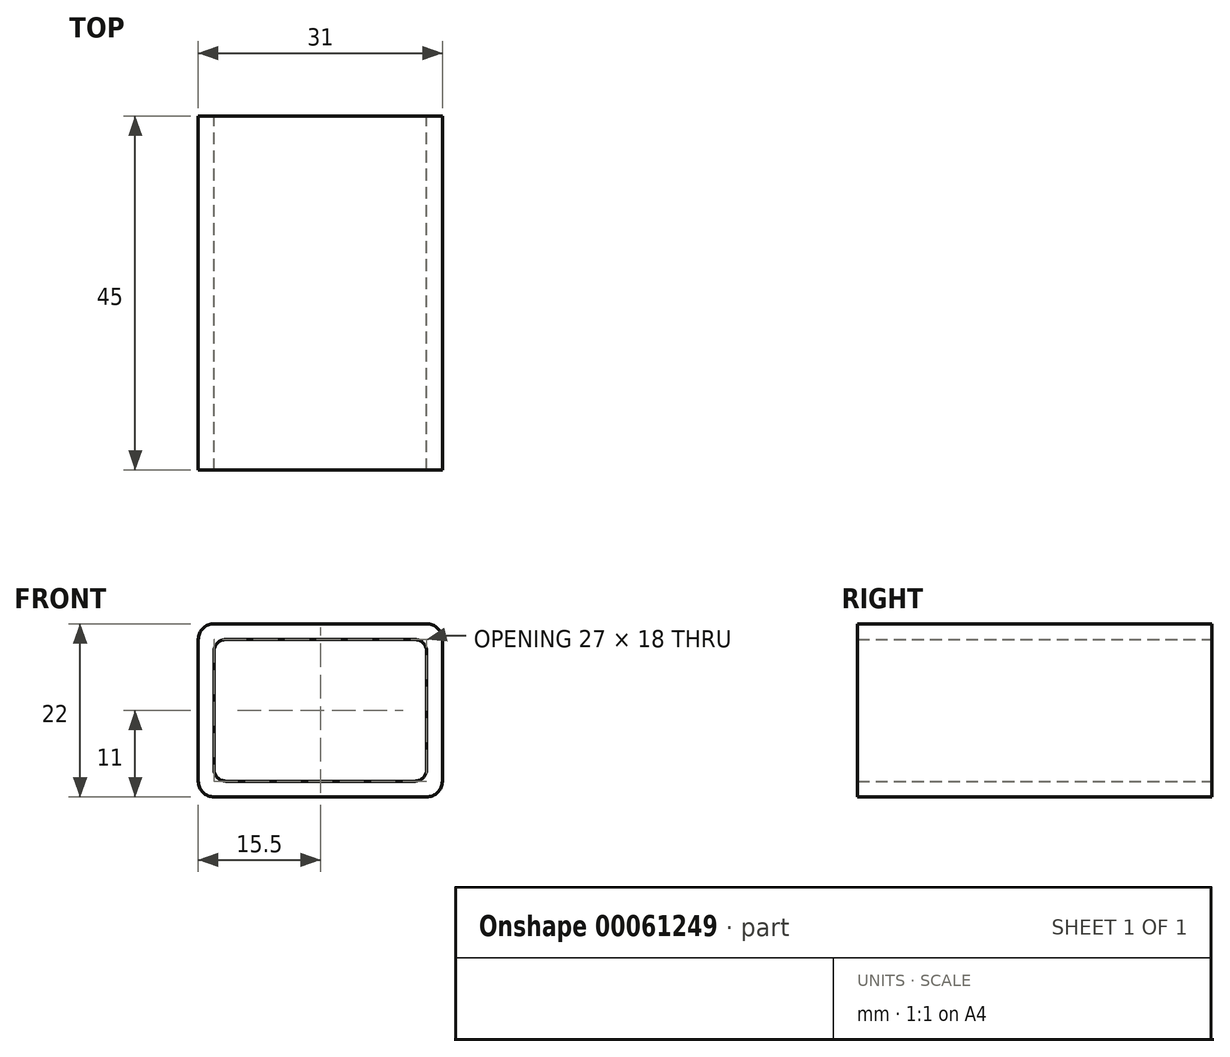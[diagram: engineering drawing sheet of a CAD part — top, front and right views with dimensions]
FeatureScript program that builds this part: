
annotation { "Feature Type Name" : "Feature", "Feature Type Description" : "" }
export const myFeature = defineFeature(function(context is Context, id is Id, definition is map)
    precondition{}
    {
        {
            var Q0;
            Q0=qCreatedBy(makeId("Front.planeOp"),FACE);
            var sketch = newSketch(context, id + "F0", { "sketchPlane" : qUnion([Q0])});
            skLineSegment(sketch, "E0.bottom", {"start": v(0, 0) * mm, "end": v(27, 0) * mm});
            skLineSegment(sketch, "E0.top", {"start": v(0, 18) * mm, "end": v(27, 18) * mm});
            skLineSegment(sketch, "E0.left", {"start": v(0, 0) * mm, "end": v(0, 18) * mm});
            skLineSegment(sketch, "E0.right", {"start": v(27, 0) * mm, "end": v(27, 18) * mm});
            skLineSegment(sketch, "E1.0", {"start": v(-2, 20) * mm, "end": v(29, 20) * mm});
            skLineSegment(sketch, "E1.1", {"start": v(-2, -2) * mm, "end": v(-2, 20) * mm});
            skLineSegment(sketch, "E1.2", {"start": v(-2, -2) * mm, "end": v(29, -2) * mm});
            skLineSegment(sketch, "E1.3", {"start": v(29, -2) * mm, "end": v(29, 20) * mm});
            skSolve(sketch);
        }
        {
            var Q0;
            Q0 = qSketchRegion(id + "F0", true);
            extrude(context, id + "F1", {"entities" : qUnion([Q0]), "depth" : 45 * mm});
        }
        {
            var Q0;
            Q0=makeQuery(id+"F1.opExtrude","SWEPT_EDGE",EDGE,{"disambiguationData":[OSD([sQuery(id+"F0.wireOp",EDGE,"E1.0"),sQuery(id+"F0.wireOp",EDGE,"E1.3")])]});
            var Q1;
            Q1=makeQuery(id+"F1.opExtrude","SWEPT_EDGE",EDGE,{"disambiguationData":[OSD([sQuery(id+"F0.wireOp",EDGE,"E1.0"),sQuery(id+"F0.wireOp",EDGE,"E1.1")])]});
            var Q2;
            Q2=makeQuery(id+"F1.opExtrude","SWEPT_EDGE",EDGE,{"disambiguationData":[OSD([sQuery(id+"F0.wireOp",EDGE,"E1.2"),sQuery(id+"F0.wireOp",EDGE,"E1.3")])]});
            var Q3;
            Q3=makeQuery(id+"F1.opExtrude","SWEPT_EDGE",EDGE,{"disambiguationData":[OSD([sQuery(id+"F0.wireOp",EDGE,"E1.1"),sQuery(id+"F0.wireOp",EDGE,"E1.2")])]});
            fillet(context, id + "F2", {"entities" : qUnion([Q0, Q1, Q2, Q3]), "radius" : 2 * mm, "tangentPropagation" : true, "allowEdgeOverflow" : false});
        }
        {
            var Q0;
            Q0=makeQuery(id+"F1.opExtrude","SWEPT_EDGE",EDGE,{"disambiguationData":[OSD([sQuery(id+"F0.wireOp",EDGE,"E0.top"),sQuery(id+"F0.wireOp",EDGE,"E0.right")])]});
            var Q1;
            Q1=makeQuery(id+"F1.opExtrude","SWEPT_EDGE",EDGE,{"disambiguationData":[OSD([sQuery(id+"F0.wireOp",EDGE,"E0.bottom"),sQuery(id+"F0.wireOp",EDGE,"E0.right")])]});
            var Q2;
            Q2=makeQuery(id+"F1.opExtrude","SWEPT_EDGE",EDGE,{"disambiguationData":[OSD([sQuery(id+"F0.wireOp",EDGE,"E0.bottom"),sQuery(id+"F0.wireOp",EDGE,"E0.left")])]});
            var Q3;
            Q3=makeQuery(id+"F1.opExtrude","SWEPT_EDGE",EDGE,{"disambiguationData":[OSD([sQuery(id+"F0.wireOp",EDGE,"E0.top"),sQuery(id+"F0.wireOp",EDGE,"E0.left")])]});
            fillet(context, id + "F3", {"entities" : qUnion([Q0, Q1, Q2, Q3]), "radius" : 1.5 * mm, "tangentPropagation" : true, "allowEdgeOverflow" : false});
        }
    });
